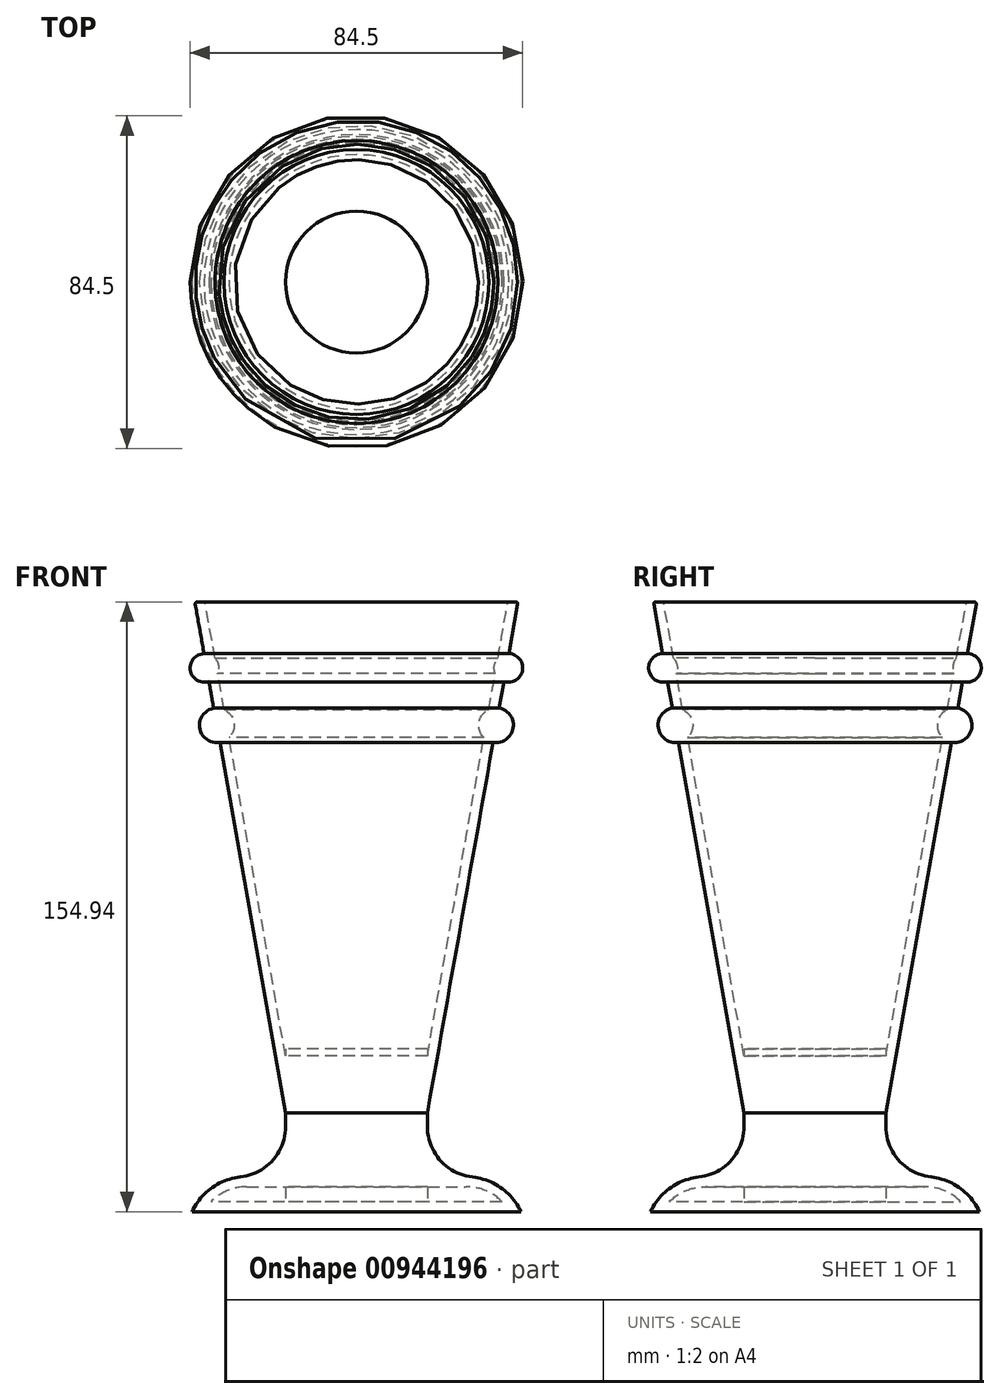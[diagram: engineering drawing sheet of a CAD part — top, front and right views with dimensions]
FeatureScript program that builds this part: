
annotation { "Feature Type Name" : "Feature", "Feature Type Description" : "" }
export const myFeature = defineFeature(function(context is Context, id is Id, definition is map)
    precondition{}
    {
        {
            var Q0;
            Q0=qCreatedBy(makeId("Top.planeOp"),FACE);
            var sketch = newSketch(context, id + "F0", { "sketchPlane" : qUnion([Q0])});
            skCircle(sketch, "E0", {"center": v(0, 0) * mm, "radius": 13.57 * mm});
            skSolve(sketch);
        }
        {
            var Q0;
            Q0=qCreatedBy(makeId("Top.planeOp"),FACE);
            cPlane(context, id + "F1", {"entities" : qUnion([Q0]), "cplaneType" : CPlaneType.OFFSET, "offset" : 154.94 * mm, "width" : 152.4 * mm, "height" : 152.4 * mm});
        }
        {
            var Q0;
            Q0=qCreatedBy(id+"F1.planeOp",FACE);
            var sketch = newSketch(context, id + "F2", { "sketchPlane" : qUnion([Q0])});
            skCircle(sketch, "E1", {"center": v(0, 0) * mm, "radius": 41.06 * mm});
            skSolve(sketch);
        }
        {
            var Q0;
            Q0=makeQuery(id+"F2.imprint","IMPRINT",FACE,{"disambiguationData":[TD([[makeQuery(id+"F2.imprint","IMPRINT",EDGE,{"derivedFrom":sQuery(id+"F2.wireOp",EDGE,"E1")}),1.0]])]});
            var Q1;
            Q1=makeQuery(id+"F0.imprint","IMPRINT",FACE,{"disambiguationData":[TD([[makeQuery(id+"F0.imprint","IMPRINT",EDGE,{"derivedFrom":sQuery(id+"F0.wireOp",EDGE,"E0")}),1.0]])]});
            loft(context, id + "F3", {"sheetProfilesArray" : [{ "sheetProfileEntities" : qUnion([Q0]) }, { "sheetProfileEntities" : qUnion([Q1]) }]});
        }
        {
            var Q0;
            Q0=qCreatedBy(makeId("Top.planeOp"),FACE);
            var sketch = newSketch(context, id + "F4", { "sketchPlane" : qUnion([Q0])});
            skCircle(sketch, "E2", {"center": v(0, 0) * mm, "radius": 41.78 * mm});
            skSolve(sketch);
        }
        {
            var Q0;
            Q0=makeQuery(id+"F4.imprint","IMPRINT",FACE,{"disambiguationData":[TD([[makeQuery(id+"F4.imprint","IMPRINT",EDGE,{"derivedFrom":sQuery(id+"F4.wireOp",EDGE,"E2")}),1.0]])]});
            extrude(context, id + "F5", {"entities" : qUnion([Q0]), "operationType" : NewBodyOperationType.ADD, "depth" : 8.9 * mm, "offsetDistance" : 25.4 * mm});
        }
        {
            var Q0;
            Q0=makeQuery(id+"F5.opExtrude","CAP_EDGE",EDGE,{"disambiguationData":[OSD([sQuery(id+"F4.wireOp",EDGE,"E2")])],"isStart":false});
            fillet(context, id + "F6", {"entities" : qUnion([Q0]), "radius" : 15.33 * mm, "tangentPropagation" : true, "allowEdgeOverflow" : false});
        }
        {
            var Q0;
            Q0=makeQuery(id+"F3.opLoft","CAP_FACE",FACE,{"disambiguationData":[OSD([makeQuery(id+"F2.imprint","IMPRINT",FACE,{"disambiguationData":[TD([[makeQuery(id+"F2.imprint","IMPRINT",EDGE,{"derivedFrom":sQuery(id+"F2.wireOp",EDGE,"E1")}),1.0]])]})])],"isStart":true});
            shell(context, id + "F7", {"entities" : qUnion([Q0]), "thickness" : 2.54 * mm});
        }
        {
            var Q0;
            Q0=qCreatedBy(makeId("Top.planeOp"),FACE);
            var sketch = newSketch(context, id + "F8", { "sketchPlane" : qUnion([Q0])});
            skCircle(sketch, "E3", {"center": v(0, 0) * mm, "radius": 18.01 * mm});
            skSolve(sketch);
        }
        {
            var Q0;
            Q0 = qSketchRegion(id + "F8", true);
            extrude(context, id + "F9", {"entities" : qUnion([Q0]), "operationType" : NewBodyOperationType.ADD, "depth" : 41.4 * mm, "offsetDistance" : 25.4 * mm});
        }
        {
            var Q0;
            Q0=qCreatedBy(makeId("Front.planeOp"),FACE);
            var sketch = newSketch(context, id + "F10", { "sketchPlane" : qUnion([Q0])});
            skCircle(sketch, "E4", {"center": v(-35.47, 123.58) * mm, "radius": 4.4 * mm});
            skCircle(sketch, "E5", {"center": v(-38.62, 138.17) * mm, "radius": 3.63 * mm});
            skSolve(sketch);
        }
        {
            var Q0;
            Q0=makeQuery(id+"F10.imprint","IMPRINT",FACE,{"disambiguationData":[TD([[makeQuery(id+"F10.imprint","IMPRINT",EDGE,{"derivedFrom":sQuery(id+"F10.wireOp",EDGE,"E5")}),1.0]])]});
            var Q1;
            {var subQ0=sQuery(id+"F4.wireOp",EDGE,"E2");Q1=makeQuery(id+"F6.opFillet","BLEND_EDGE",EDGE,{"blendedFrom":[makeQuery(id+"F5.opExtrude","CAP_EDGE",EDGE,{"disambiguationData":[OSD([subQ0])],"isStart":false}),makeQuery(id+"F5.boolean.opBoolean","MERGE",FACE,{"derivedFrom":[makeQuery(id+"F3.opLoft","CAP_FACE",FACE,{"disambiguationData":[OSD([makeQuery(id+"F0.imprint","IMPRINT",FACE,{"disambiguationData":[TD([[makeQuery(id+"F0.imprint","IMPRINT",EDGE,{"derivedFrom":sQuery(id+"F0.wireOp",EDGE,"E0")}),1.0]])]})])],"isStart":true}),makeQuery(id+"F5.opExtrude","CAP_FACE",FACE,{"disambiguationData":[OSD([subQ0])],"isStart":true})]})],"blendedInto":[makeQuery(id+"F5.boolean.opBoolean","MERGE",FACE,{"derivedFrom":[makeQuery(id+"F3.opLoft","CAP_FACE",FACE,{"disambiguationData":[OSD([makeQuery(id+"F0.imprint","IMPRINT",FACE,{"disambiguationData":[TD([[makeQuery(id+"F0.imprint","IMPRINT",EDGE,{"derivedFrom":sQuery(id+"F0.wireOp",EDGE,"E0")}),1.0]])]})])],"isStart":true}),makeQuery(id+"F5.opExtrude","CAP_FACE",FACE,{"disambiguationData":[OSD([subQ0])],"isStart":true})]})]});}
            revolve(context, id + "F11", {"operationType" : NewBodyOperationType.ADD, "surfaceOperationType" : NewSurfaceOperationType.NEW, "entities" : qUnion([Q0]), "axis" : qUnion([Q1]), "revolveType" : RevolveType.FULL});
        }
        {
            var Q0;
            Q0 = qSketchRegion(id + "F10", true);
            var Q1;
            {var subQ0=sQuery(id+"F4.wireOp",EDGE,"E2");Q1=makeQuery(id+"F6.opFillet","BLEND_EDGE",EDGE,{"blendedFrom":[makeQuery(id+"F5.opExtrude","CAP_EDGE",EDGE,{"disambiguationData":[OSD([subQ0])],"isStart":false}),makeQuery(id+"F5.boolean.opBoolean","MERGE",FACE,{"derivedFrom":[makeQuery(id+"F3.opLoft","CAP_FACE",FACE,{"disambiguationData":[OSD([makeQuery(id+"F0.imprint","IMPRINT",FACE,{"disambiguationData":[TD([[makeQuery(id+"F0.imprint","IMPRINT",EDGE,{"derivedFrom":sQuery(id+"F0.wireOp",EDGE,"E0")}),1.0]])]})])],"isStart":true}),makeQuery(id+"F5.opExtrude","CAP_FACE",FACE,{"disambiguationData":[OSD([subQ0])],"isStart":true})]})],"blendedInto":[makeQuery(id+"F5.boolean.opBoolean","MERGE",FACE,{"derivedFrom":[makeQuery(id+"F3.opLoft","CAP_FACE",FACE,{"disambiguationData":[OSD([makeQuery(id+"F0.imprint","IMPRINT",FACE,{"disambiguationData":[TD([[makeQuery(id+"F0.imprint","IMPRINT",EDGE,{"derivedFrom":sQuery(id+"F0.wireOp",EDGE,"E0")}),1.0]])]})])],"isStart":true}),makeQuery(id+"F5.opExtrude","CAP_FACE",FACE,{"disambiguationData":[OSD([subQ0])],"isStart":true})]})]});}
            revolve(context, id + "F12", {"operationType" : NewBodyOperationType.ADD, "surfaceOperationType" : NewSurfaceOperationType.NEW, "entities" : qUnion([Q0]), "axis" : qUnion([Q1]), "revolveType" : RevolveType.FULL});
        }
        {
            var Q0;
            Q0=makeQuery(id+"F7.opShell","OFFSET_EDGE",EDGE,{"disambiguationData":[OSD([sQuery(id+"F2.wireOp",EDGE,"E1")])]});
            var Q1;
            Q1=makeQuery(id+"F3.opLoft","MID_CAP_EDGE",EDGE,{"disambiguationData":[OSD([sQuery(id+"F2.wireOp",EDGE,"E1")])],"capPos":0.0});
            fillet(context, id + "F13", {"entities" : qUnion([Q0, Q1]), "radius" : 0.5 * mm, "tangentPropagation" : true, "allowEdgeOverflow" : false});
        }
        {
            var Q0;
            Q0=makeQuery(id+"F9.boolean.opBoolean","INTERSECT",EDGE,{"derivedFrom":[makeQuery(id+"F5.opExtrude","CAP_FACE",FACE,{"disambiguationData":[OSD([sQuery(id+"F4.wireOp",EDGE,"E2")])],"isStart":false}),makeQuery(id+"F9.opExtrude","SWEPT_FACE",FACE,{"disambiguationData":[OSD([sQuery(id+"F8.wireOp",EDGE,"E3")])]})]});
            fillet(context, id + "F14", {"entities" : qUnion([Q0]), "radius" : 12.88 * mm, "tangentPropagation" : true, "allowEdgeOverflow" : false});
        }
    });
